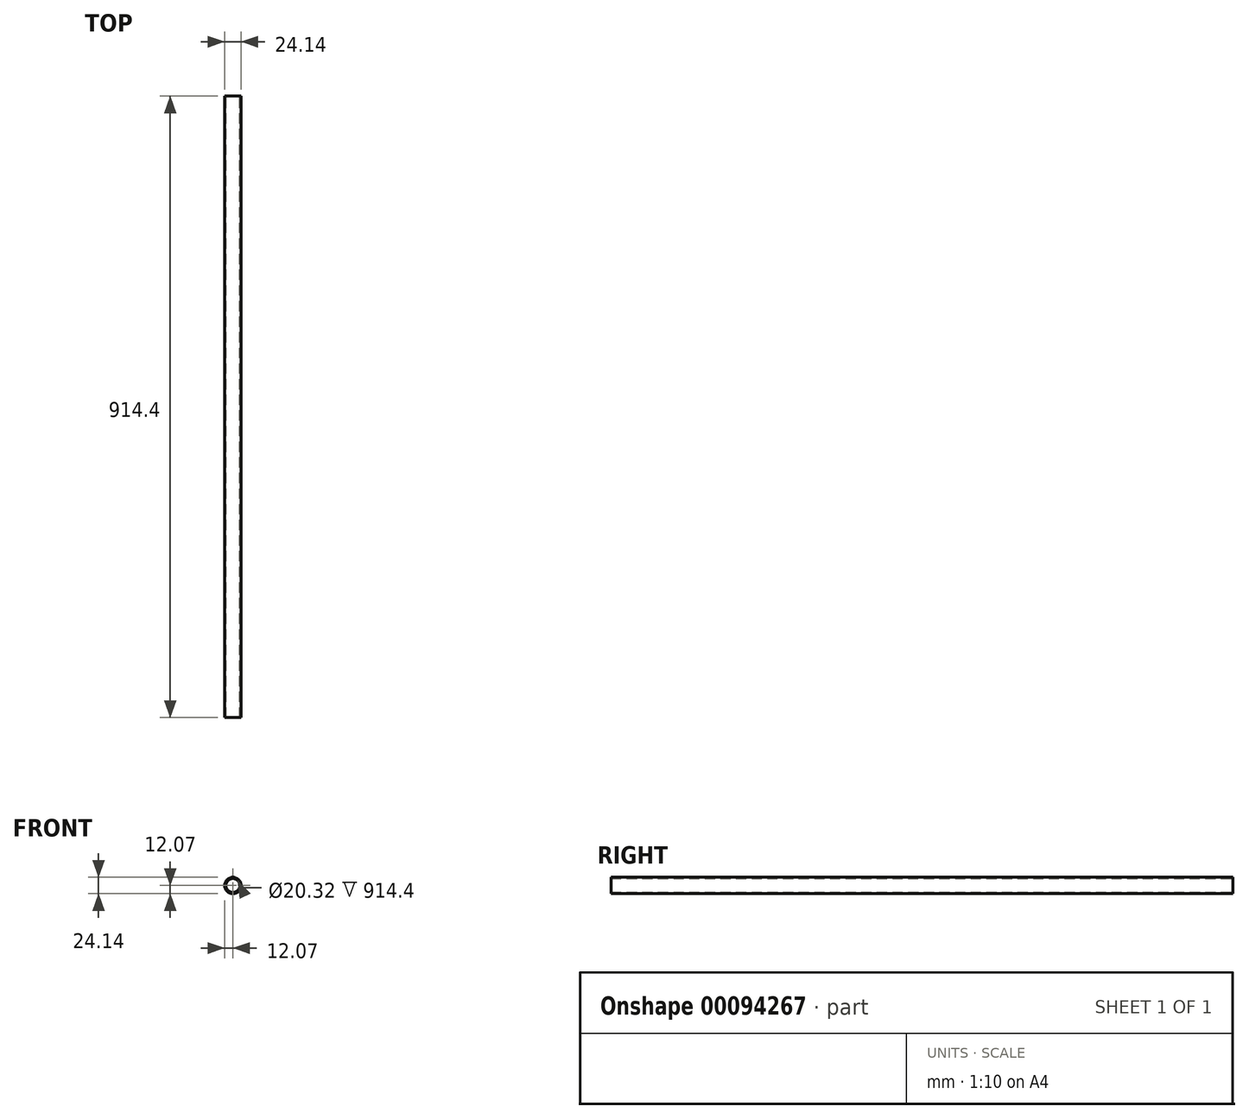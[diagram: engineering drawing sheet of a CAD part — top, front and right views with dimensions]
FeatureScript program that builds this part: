
annotation { "Feature Type Name" : "Feature", "Feature Type Description" : "" }
export const myFeature = defineFeature(function(context is Context, id is Id, definition is map)
    precondition{}
    {
        {
            var Q0;
            Q0=qCreatedBy(makeId("Front.planeOp"),FACE);
            var sketch = newSketch(context, id + "F0", { "sketchPlane" : qUnion([Q0])});
            skCircle(sketch, "E0", {"center": v(0, 0) * mm, "radius": 12.07 * mm});
            skCircle(sketch, "E1", {"center": v(0, 0) * mm, "radius": 10.16 * mm});
            skSolve(sketch);
        }
        {
            var Q0;
            Q0=makeQuery(id+"F0.imprint","IMPRINT",FACE,{"disambiguationData":[TD([[makeQuery(id+"F0.imprint","IMPRINT",EDGE,{"derivedFrom":sQuery(id+"F0.wireOp",EDGE,"E0")}),1.0]])]});
            extrude(context, id + "F1", {"entities" : qUnion([Q0]), "endBound" : BoundingType.SYMMETRIC, "depth" : 914.4 * mm});
        }
    });
